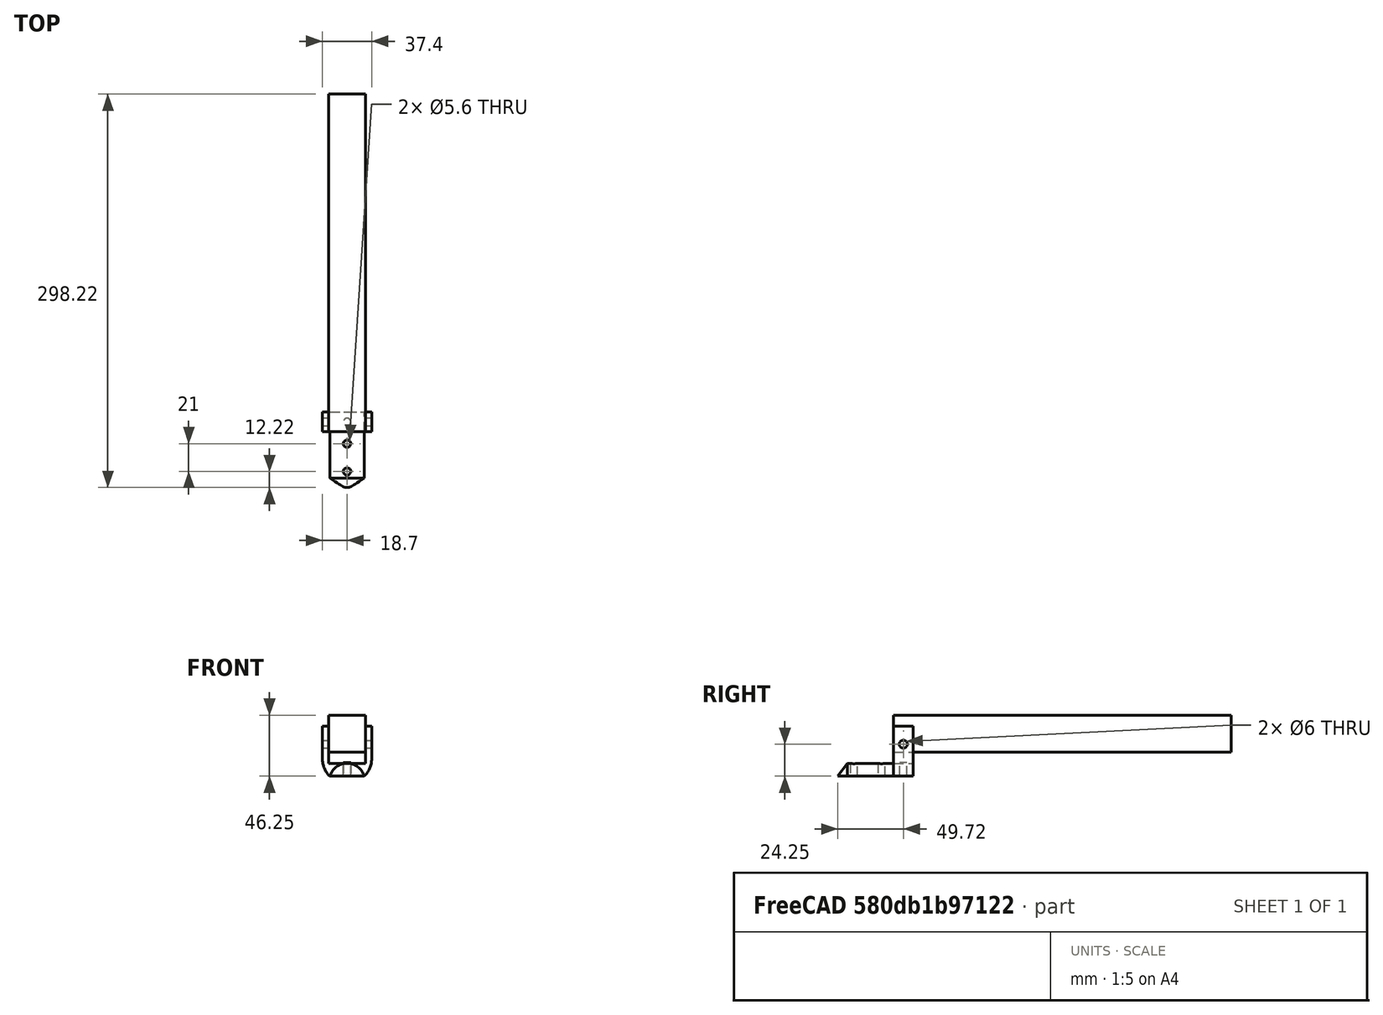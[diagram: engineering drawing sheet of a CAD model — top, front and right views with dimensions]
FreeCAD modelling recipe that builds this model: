
FCSTD DOCUMENT  (FreeCAD 0.20R29410 (Git))
Label: outerLook07122022
License: All rights reserved
LicenseURL: http://en.wikipedia.org/wiki/All_rights_reserved
objects: Part::Cylinder×6, Part::Box×5, Part::Cut×4, Part::MultiFuse×4, Part::Cone×1, Part::MultiCommon×1
note: 21 computed .brp shape members not serialized (recipe doc carries the construction recipe); baked Part::Feature solids carry a one-line shape summary decoded from their .brp

FEATURE [Part::Cylinder] Cylinder
  Angle = 360
  AttacherType = Attacher::AttachEngine3D
  FirstAngle = 0
  Height = 50
  Placement = pos=(13.5,-5,43) rot=(-1,0,0;1.5708rad)
  Radius = 13.5
  SecondAngle = 0
FEATURE [Part::Box] Box  label="TSlotFrameCut"
  AttacherType = Attacher::AttachEngine3D
  Height = 28
  Length = 28
  Placement = pos=(-0.5,30,65) rot=(0,0,1;0rad)
  Width = 256
FEATURE [Part::Box] Box015  label="TSlotMount001"
  AttacherType = Attacher::AttachEngine3D
  Height = 37.75
  Length = 37.4
  Placement = pos=(-5.2,30,46.75) rot=(0,0,1;0rad)
  Width = 15
FEATURE [Part::Cylinder] Cylinder009  label="m5Cut"
  Angle = 360
  AttacherType = Attacher::AttachEngine3D
  FirstAngle = 0
  Height = 100
  Placement = pos=(-56.4,37.5,71) rot=(0,1,0;1.5708rad)
  Radius = 3
  SecondAngle = 0
FEATURE [Part::Box] Box016  label="Shell_Holder002"
  AttacherType = Attacher::AttachEngine3D
  Height = 20
  Length = 27
  Placement = pos=(0,-20.5,26.75) rot=(0,0,1;0rad)
  Width = 75
FEATURE [Part::Cylinder] Cylinder011
  Angle = 360
  AttacherType = Attacher::AttachEngine3D
  FirstAngle = 0
  Height = 12
  Placement = pos=(13.5,0,45) rot=(0,0,1;1.5708rad)
  Radius = 2.8
  SecondAngle = 0
FEATURE [Part::Cylinder] Cylinder012
  Angle = 360
  AttacherType = Attacher::AttachEngine3D
  FirstAngle = 0
  Height = 10
  Placement = pos=(13.5,37.5,47) rot=(0,0,1;1.5708rad)
  Radius = 2.8
  SecondAngle = 0
FEATURE [Part::Box] Box018  label="TSlotFrameCut001"
  AttacherType = Attacher::AttachEngine3D
  Height = 28
  Length = 28
  Placement = pos=(-0.5,0,56.5) rot=(0,0,1;0rad)
  Width = 254
FEATURE [Part::Cut] Cut009  label="TSlotMount002"
  Base = -> Box015
  Tool = -> Box018
FEATURE [Part::Cylinder] Cylinder015
  Angle = 360
  AttacherType = Attacher::AttachEngine3D
  FirstAngle = 0
  Height = 12
  Placement = pos=(13.5,21,45) rot=(0,0,1;1.5708rad)
  Radius = 2.8
  SecondAngle = 0
FEATURE [Part::Cone] Cone
  Angle = 180
  AttacherType = Attacher::AttachEngine3D
  Height = 10
  Placement = pos=(13.5,-5,43) rot=(1,0,0;1.5708rad)
  Radius1 = 13.5
  Radius2 = 0
FEATURE [Part::MultiFuse] Fusion  label="beak"
  Shapes = -> [Cylinder,Cone]
FEATURE [Part::Cut] Cut
  Base = -> Fusion
  Tool = -> Box016
FEATURE [Part::MultiFuse] Fusion001  label="heatSetCuts"
  Shapes = -> [Cylinder011,Cylinder015]
FEATURE [Part::Cut] Cut010
  Base = -> Cut009
  Tool = -> Cylinder009
FEATURE [Part::MultiFuse] Fusion002
  Shapes = -> [Cut,Cut010]
FEATURE [Part::Cut] Cut011
  Base = -> Fusion002
  Tool = -> Fusion001
FEATURE [Part::Cylinder] Cylinder016  label="reshapes"
  Angle = 360
  AttacherType = Attacher::AttachEngine3D
  FirstAngle = 0
  Height = 63
  Placement = pos=(13.5,45,60) rot=(1,0,0;1.5708rad)
  Radius = 18.7
  SecondAngle = 0
FEATURE [Part::Box] Box019  label="reshapes001"
  AttacherType = Attacher::AttachEngine3D
  Height = 29
  Length = 40
  Placement = pos=(-6.5,30,60) rot=(0,0,1;0rad)
  Width = 18
FEATURE [Part::MultiFuse] Fusion003
  Shapes = -> [Box019,Cylinder016]
FEATURE [Part::MultiCommon] Common
  Shapes = -> [Fusion003,Cut011]
